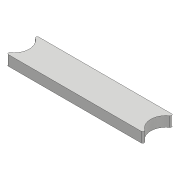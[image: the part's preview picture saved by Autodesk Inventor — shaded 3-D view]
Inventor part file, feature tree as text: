
AUTODESK INVENTOR PART (.ipt)
format: ipt  version: 2018 (Build 220112000, 112)  size: 86,016 bytes
history: native  units: mm
features: extrude x1, fillet x1, sketch x1
ambient origin geometry x8: Origin, YZ Plane, XZ Plane, XY Plane, X Axis, Y Axis, Z Axis, Center Point
bodies: Body1 (feature_tree)
feature tree (3):
  extrude  "Extrusion2"  Depth=300.0mm
  fillet  "Fillet2"  Radius=60.0mm
  sketch  "Sketch1"  dims[d6=60.0mm d7=300.0mm d8=60.0mm d9=20.0mm d10=0.0mm d11=3.0mm]
